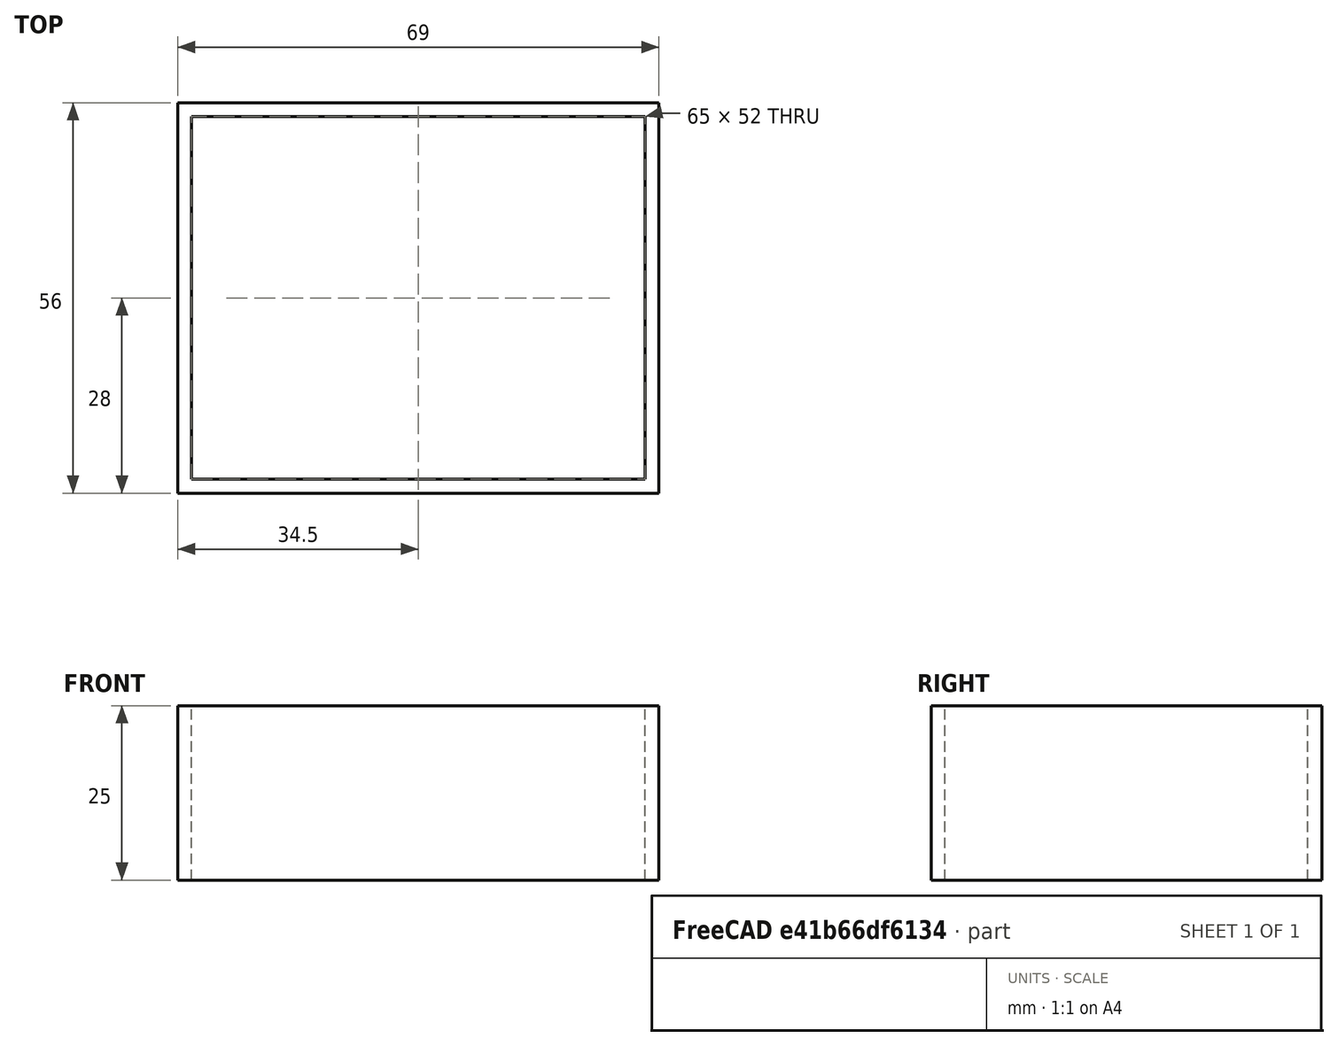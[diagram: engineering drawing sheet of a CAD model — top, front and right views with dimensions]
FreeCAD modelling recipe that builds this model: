
FCSTD DOCUMENT  (FreeCAD 0.20R29177 +426 (Git))
Label: extender
License: All rights reserved
LicenseURL: http://en.wikipedia.org/wiki/All_rights_reserved
objects: Sketcher::SketchObject×1, PartDesign::Pad×1, PartDesign::Body×1
note: 4 computed .brp shape members not serialized (recipe doc carries the construction recipe); baked Part::Feature solids carry a one-line shape summary decoded from their .brp

FEATURE [Sketcher::SketchObject] Sketch
  FullyConstrained = true
  MapMode = 5
  Support = -> [XY_Plane]
  sketch-geometry (8):
    g0: LineSegment StartX=-34.5 StartY=28 StartZ=0 EndX=34.5 EndY=28 EndZ=0
    g1: LineSegment StartX=34.5 StartY=28 StartZ=0 EndX=34.5 EndY=-28 EndZ=0
    g2: LineSegment StartX=34.5 StartY=-28 StartZ=0 EndX=-34.5 EndY=-28 EndZ=0
    g3: LineSegment StartX=-34.5 StartY=-28 StartZ=0 EndX=-34.5 EndY=28 EndZ=0
    g4: LineSegment StartX=-32.5 StartY=26 StartZ=0 EndX=32.5 EndY=26 EndZ=0
    g5: LineSegment StartX=32.5 StartY=26 StartZ=0 EndX=32.5 EndY=-26 EndZ=0
    g6: LineSegment StartX=32.5 StartY=-26 StartZ=0 EndX=-32.5 EndY=-26 EndZ=0
    g7: LineSegment StartX=-32.5 StartY=-26 StartZ=0 EndX=-32.5 EndY=26 EndZ=0
  constraints (22):
    c: Coincident(g0,g1)
    c: Coincident(g1,g2)
    c: Coincident(g2,g3)
    c: Coincident(g3,g0)
    c: Horizontal(g0)
    c: Horizontal(g2)
    c: Vertical(g1)
    c: Vertical(g3)
    c: DistanceX(g0,g0) = 69
    c: DistanceY(g3,g3) = 56
    c: Symmetric(g2,g0,g-1)
    c: Coincident(g4,g5)
    c: Coincident(g5,g6)
    c: Coincident(g6,g7)
    c: Coincident(g7,g4)
    c: Horizontal(g4)
    c: Horizontal(g6)
    c: Vertical(g5)
    c: Vertical(g7)
    c: DistanceX(g4,g4) = 65
    c: DistanceY(g7,g7) = 52
    c: Symmetric(g4,g5,g-1)
FEATURE [PartDesign::Pad] Pad
  Direction = (0,0,1)
  Length = 25
  Length2 = 10
  Profile = -> Sketch
  ReferenceAxis = -> Sketch [N_Axis]
  Type = 0
FEATURE [PartDesign::Body] Body
  Group = -> [Sketch,Pad]
  Origin = -> Origin
  Tip = -> Pad
